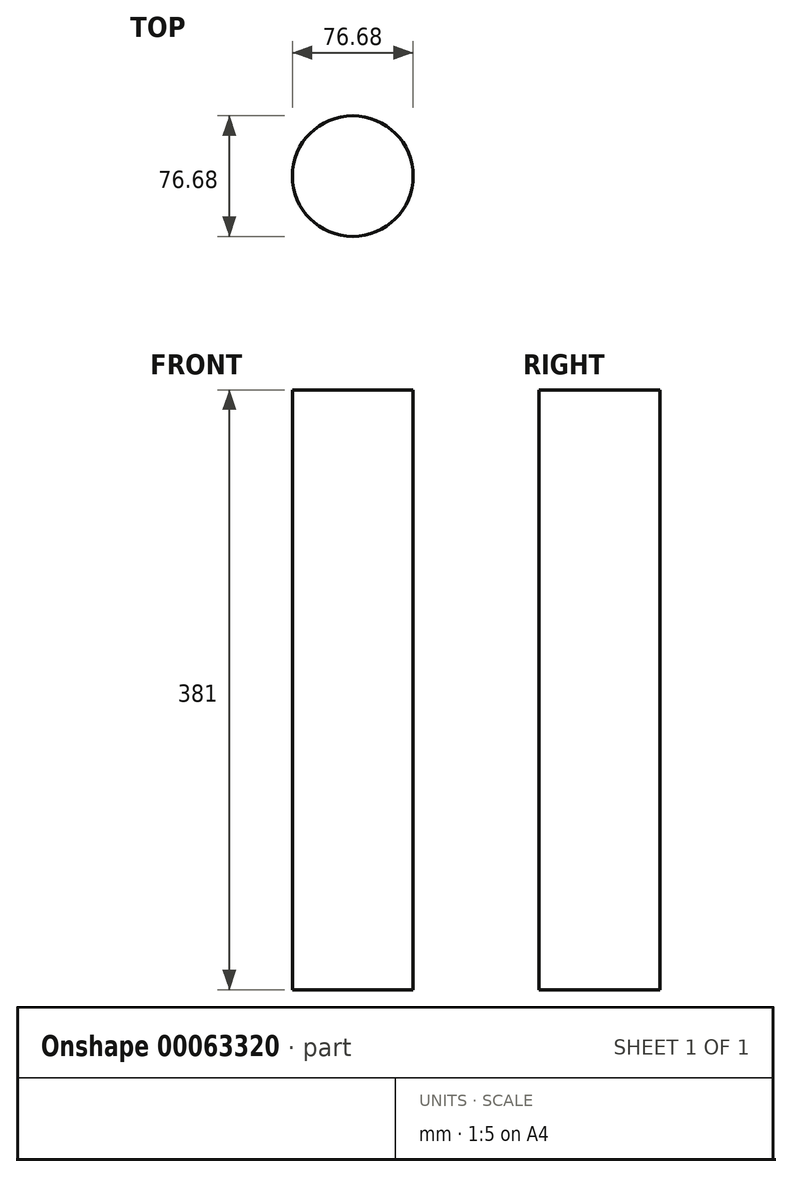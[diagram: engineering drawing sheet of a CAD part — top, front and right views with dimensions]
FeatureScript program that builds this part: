
annotation { "Feature Type Name" : "Feature", "Feature Type Description" : "" }
export const myFeature = defineFeature(function(context is Context, id is Id, definition is map)
    precondition{}
    {
        {
            var Q0;
            Q0=qCreatedBy(makeId("Top.planeOp"),FACE);
            var sketch = newSketch(context, id + "F0", { "sketchPlane" : qUnion([Q0])});
            skCircle(sketch, "E0", {"center": v(0, 0) * mm, "radius": 38.34 * mm});
            skSolve(sketch);
        }
        {
            var Q0;
            Q0=makeQuery(id+"F0.imprint","IMPRINT",FACE,{"disambiguationData":[TD([[makeQuery(id+"F0.imprint","IMPRINT",EDGE,{"derivedFrom":sQuery(id+"F0.wireOp",EDGE,"E0")}),1.0]])]});
            extrude(context, id + "F1", {"entities" : qUnion([Q0]), "depth" : 381 * mm});
        }
    });
